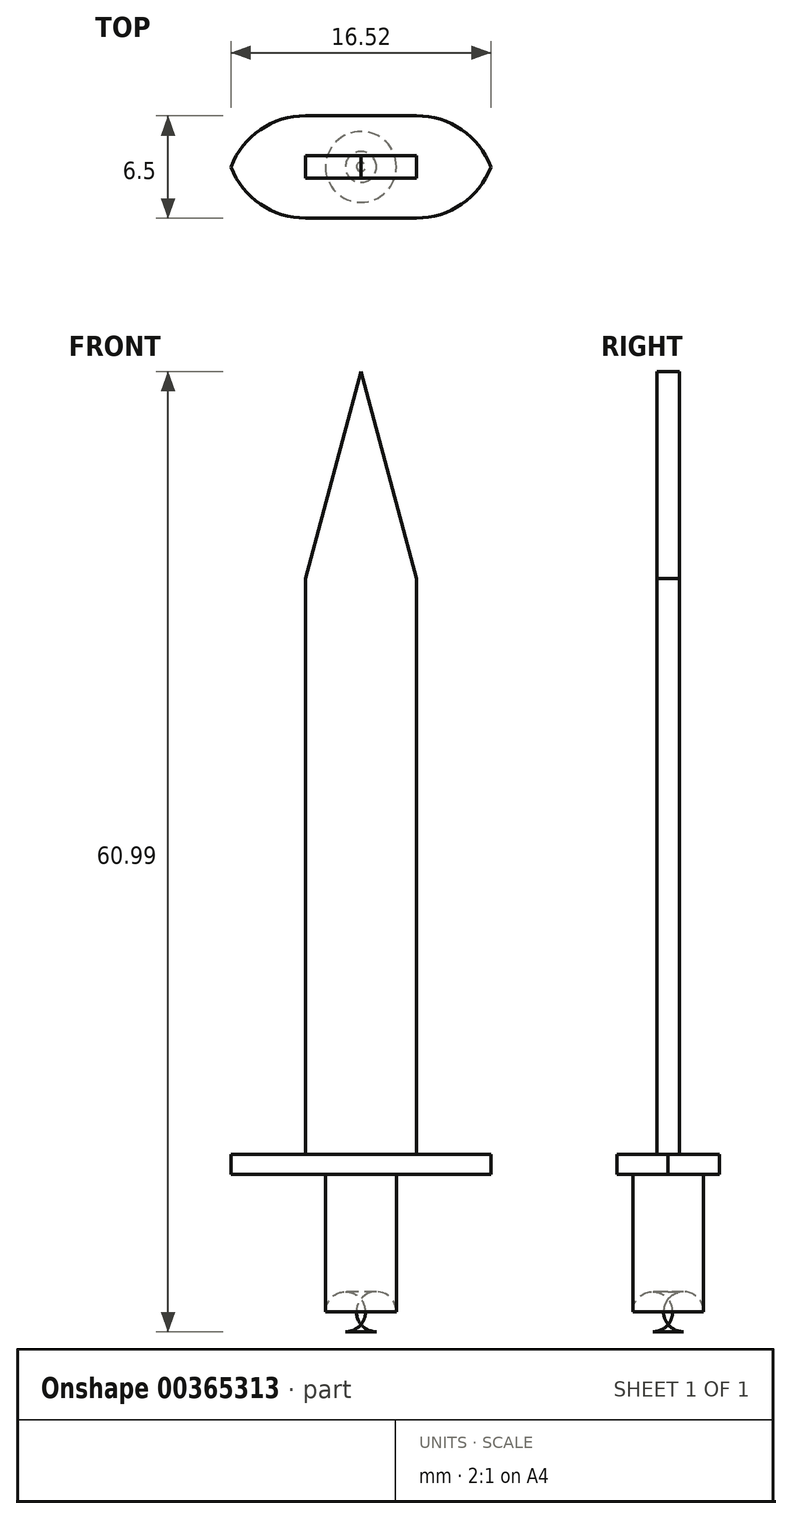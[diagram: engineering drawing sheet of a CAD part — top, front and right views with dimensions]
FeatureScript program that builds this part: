
annotation { "Feature Type Name" : "Feature", "Feature Type Description" : "" }
export const myFeature = defineFeature(function(context is Context, id is Id, definition is map)
    precondition{}
    {
        {
            var Q0;
            Q0=qCreatedBy(makeId("Top.planeOp"),FACE);
            var sketch = newSketch(context, id + "F0", { "sketchPlane" : qUnion([Q0])});
            skCircle(sketch, "E0", {"center": v(0, 0) * mm, "radius": 2.25 * mm});
            skSolve(sketch);
        }
        {
            var Q0;
            Q0 = qSketchRegion(id + "F0", true);
            extrude(context, id + "F1", {"entities" : qUnion([Q0]), "depth" : 10 * mm});
        }
        {
            var Q0;
            Q0=makeQuery(id+"F1.opExtrude","CAP_FACE",FACE,{"disambiguationData":[OSD([sQuery(id+"F0.wireOp",EDGE,"E0")])],"isStart":false});
            var sketch = newSketch(context, id + "F2", { "sketchPlane" : qUnion([Q0])});
            skLineSegment(sketch, "E1.bottom", {"start": v(-8.6, 3.25) * mm, "end": v(8.6, 3.25) * mm});
            skLineSegment(sketch, "E1.top", {"start": v(-8.6, -3.25) * mm, "end": v(8.6, -3.25) * mm});
            skLineSegment(sketch, "E1.left", {"start": v(-8.6, 3.25) * mm, "end": v(-8.6, -3.25) * mm});
            skLineSegment(sketch, "E1.right", {"start": v(8.6, 3.25) * mm, "end": v(8.6, -3.25) * mm});
            skPoint(sketch, "E1.middle", {"position": v(0, 0) * mm});
            skSolve(sketch);
        }
        {
            var Q0;
            Q0=makeQuery(id+"F2.imprint","IMPRINT",FACE,{"disambiguationData":[TD([[makeQuery(id+"F2.imprint","IMPRINT",EDGE,{"derivedFrom":sQuery(id+"F2.wireOp",EDGE,"E1.bottom")}),-1.0]])]});
            var Q1;
            Q1=makeQuery(id+"F2.imprint","IMPRINT",FACE,{"disambiguationData":[TD([[makeQuery(id+"F2.imprint","IMPRINT",EDGE,{"derivedFrom":makeQuery(id+"F1.opExtrude","CAP_EDGE",EDGE,{"disambiguationData":[OSD([sQuery(id+"F0.wireOp",EDGE,"E0")])],"isStart":false})}),1.0]])]});
            extrude(context, id + "F3", {"entities" : qUnion([Q0, Q1]), "operationType" : NewBodyOperationType.ADD, "depth" : 1.27 * mm});
        }
        {
            var Q0;
            Q0=makeQuery(id+"F3.opExtrude","CAP_FACE",FACE,{"disambiguationData":[OSD([sQuery(id+"F2.wireOp",EDGE,"E1.bottom"),sQuery(id+"F2.wireOp",EDGE,"E1.top"),sQuery(id+"F2.wireOp",EDGE,"E1.left"),sQuery(id+"F2.wireOp",EDGE,"E1.right")])],"isStart":false});
            var sketch = newSketch(context, id + "F4", { "sketchPlane" : qUnion([Q0])});
            skLineSegment(sketch, "E2.bottom", {"start": v(-3.52, 0.7) * mm, "end": v(3.52, 0.7) * mm});
            skLineSegment(sketch, "E2.top", {"start": v(-3.52, -0.7) * mm, "end": v(3.52, -0.7) * mm});
            skLineSegment(sketch, "E2.left", {"start": v(-3.52, 0.7) * mm, "end": v(-3.52, -0.7) * mm});
            skLineSegment(sketch, "E2.right", {"start": v(3.52, 0.7) * mm, "end": v(3.52, -0.7) * mm});
            skPoint(sketch, "E2.middle", {"position": v(0, 0) * mm});
            skSolve(sketch);
        }
        {
            var Q0;
            Q0=makeQuery(id+"F4.imprint","IMPRINT",FACE,{"disambiguationData":[TD([[makeQuery(id+"F4.imprint","IMPRINT",EDGE,{"derivedFrom":sQuery(id+"F4.wireOp",EDGE,"E2.bottom")}),-1.0]])]});
            extrude(context, id + "F5", {"entities" : qUnion([Q0]), "operationType" : NewBodyOperationType.ADD, "depth" : 50.8 * mm});
        }
        {
            var Q0;
            Q0=makeQuery(id+"F5.opExtrude","CAP_EDGE",EDGE,{"disambiguationData":[OSD([sQuery(id+"F4.wireOp",EDGE,"E2.left")])],"isStart":false});
            var Q1;
            Q1=makeQuery(id+"F5.opExtrude","CAP_EDGE",EDGE,{"disambiguationData":[OSD([sQuery(id+"F4.wireOp",EDGE,"E2.right")])],"isStart":false});
            chamfer(context, id + "F6", {"entities" : qUnion([Q0, Q1]), "chamferType" : ChamferType.OFFSET_ANGLE, "width" : 3.8 * mm, "oppositeDirection" : false, "angle" : 75 * degree});
        }
        {
            var Q0;
            Q0=makeQuery(id+"F3.opExtrude","SWEPT_EDGE",EDGE,{"disambiguationData":[OSD([sQuery(id+"F2.wireOp",EDGE,"E1.top"),sQuery(id+"F2.wireOp",EDGE,"E1.left")])]});
            var Q1;
            Q1=makeQuery(id+"F3.opExtrude","SWEPT_EDGE",EDGE,{"disambiguationData":[OSD([sQuery(id+"F2.wireOp",EDGE,"E1.bottom"),sQuery(id+"F2.wireOp",EDGE,"E1.left")])]});
            var Q2;
            Q2=makeQuery(id+"F3.opExtrude","SWEPT_EDGE",EDGE,{"disambiguationData":[OSD([sQuery(id+"F2.wireOp",EDGE,"E1.top"),sQuery(id+"F2.wireOp",EDGE,"E1.right")])]});
            var Q3;
            Q3=makeQuery(id+"F3.opExtrude","SWEPT_EDGE",EDGE,{"disambiguationData":[OSD([sQuery(id+"F2.wireOp",EDGE,"E1.bottom"),sQuery(id+"F2.wireOp",EDGE,"E1.right")])]});
            fillet(context, id + "F7", {"entities" : qUnion([Q0, Q1, Q2, Q3]), "radius" : 5.08 * mm, "tangentPropagation" : true, "allowEdgeOverflow" : false});
        }
        {
            var Q0;
            Q0=makeQuery(id+"F1.opExtrude","CAP_EDGE",EDGE,{"disambiguationData":[OSD([sQuery(id+"F0.wireOp",EDGE,"E0")])],"isStart":true});
            fillet(context, id + "F8", {"entities" : qUnion([Q0]), "radius" : 1.27 * mm, "tangentPropagation" : true, "allowEdgeOverflow" : false});
        }
    });
